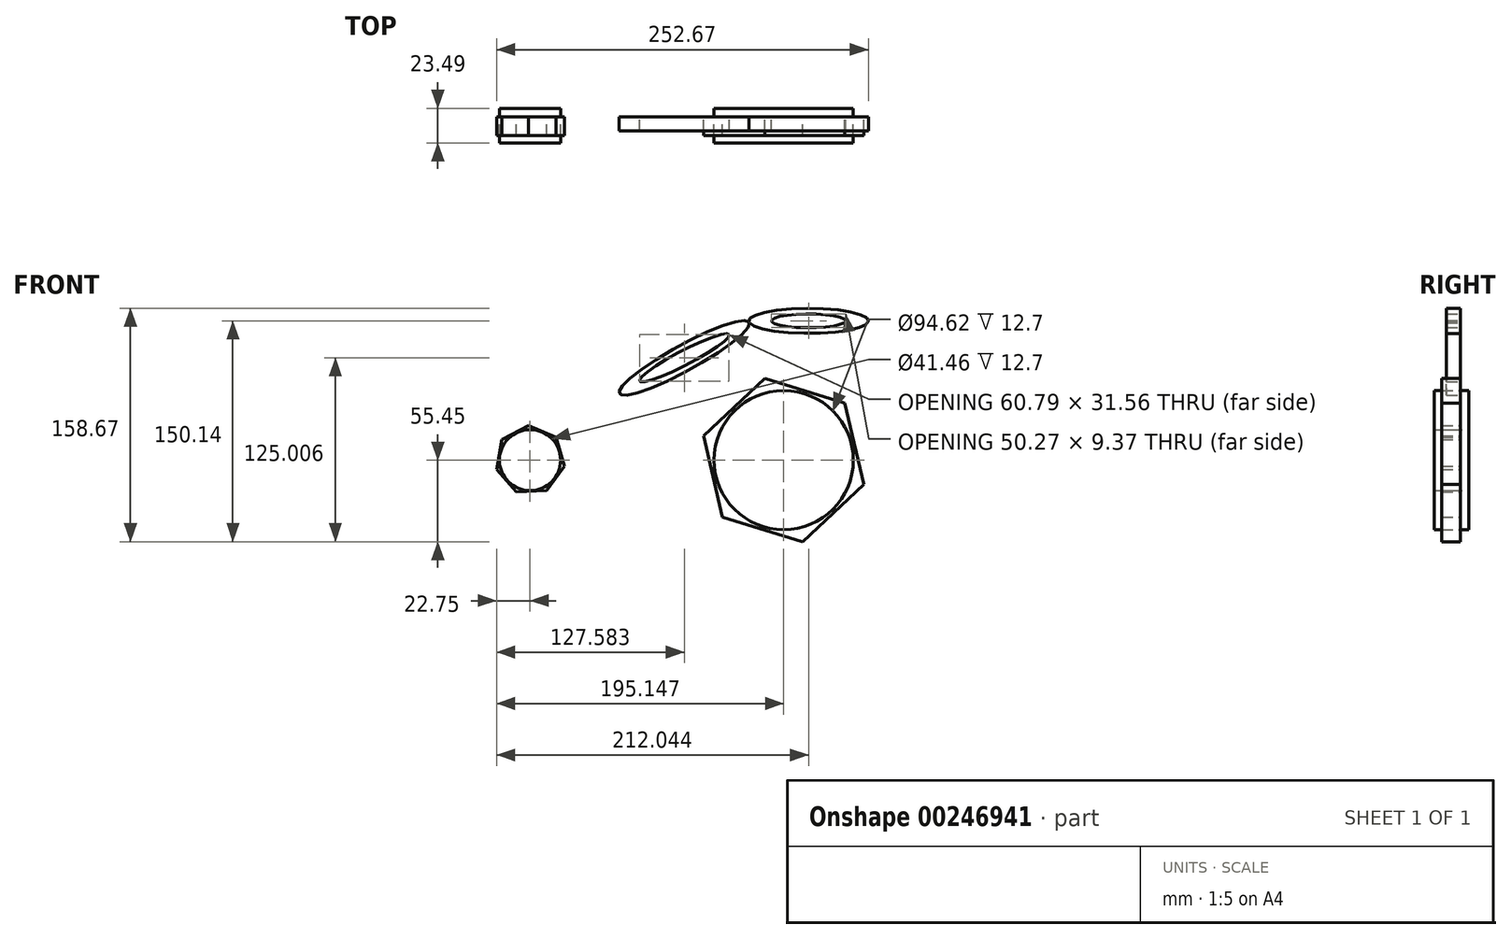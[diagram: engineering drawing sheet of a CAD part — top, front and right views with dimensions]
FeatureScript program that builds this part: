
annotation { "Feature Type Name" : "Feature", "Feature Type Description" : "" }
export const myFeature = defineFeature(function(context is Context, id is Id, definition is map)
    precondition{}
    {
        {
            var Q0;
            Q0=qCreatedBy(makeId("Front.planeOp"),FACE);
            var sketch = newSketch(context, id + "F0", { "sketchPlane" : qUnion([Q0])});
            skCircle(sketch, "E0", {"center": v(0, 0) * mm, "radius": 20.73 * mm});
            skCircle(sketch, "E1", {"center": v(172.4, 0) * mm, "radius": 47.3 * mm});
            skCircle(sketch, "E2.cCircle", {"center": v(0, 0) * mm, "radius": 23.62 * mm, "construction": true});
            skLineSegment(sketch, "E2.0", {"start": v(23.26, -4.14) * mm, "end": v(11.27, -20.76) * mm});
            skLineSegment(sketch, "E2.1", {"start": v(11.27, -20.76) * mm, "end": v(-9.2, -21.76) * mm});
            skLineSegment(sketch, "E2.2", {"start": v(-9.2, -21.76) * mm, "end": v(-22.75, -6.37) * mm});
            skLineSegment(sketch, "E2.3", {"start": v(-22.75, -6.37) * mm, "end": v(-19.16, 13.82) * mm});
            skLineSegment(sketch, "E2.4", {"start": v(-19.16, 13.82) * mm, "end": v(-1.14, 23.6) * mm});
            skLineSegment(sketch, "E2.5", {"start": v(-1.14, 23.6) * mm, "end": v(17.74, 15.6) * mm});
            skLineSegment(sketch, "E2.6", {"start": v(17.74, 15.6) * mm, "end": v(23.26, -4.14) * mm});
            skCircle(sketch, "E3.cCircle", {"center": v(172.4, 0) * mm, "radius": 56.91 * mm, "construction": true});
            skLineSegment(sketch, "E3.0", {"start": v(226.83, -16.62) * mm, "end": v(185.22, -55.45) * mm});
            skLineSegment(sketch, "E3.1", {"start": v(185.22, -55.45) * mm, "end": v(130.8, -38.83) * mm});
            skLineSegment(sketch, "E3.2", {"start": v(130.8, -38.83) * mm, "end": v(117.96, 16.62) * mm});
            skLineSegment(sketch, "E3.3", {"start": v(117.96, 16.62) * mm, "end": v(159.57, 55.45) * mm});
            skLineSegment(sketch, "E3.4", {"start": v(159.57, 55.45) * mm, "end": v(214, 38.83) * mm});
            skLineSegment(sketch, "E3.5", {"start": v(214, 38.83) * mm, "end": v(226.83, -16.62) * mm});
            skSolve(sketch);
        }
        {
            var Q0;
            Q0 = qSketchRegion(id + "F0", true);
            extrude(context, id + "F1", {"entities" : qUnion([Q0]), "depth" : 12.7 * mm});
        }
        {
            var Q0;
            Q0=makeQuery(id+"F0.imprint","IMPRINT",FACE,{"disambiguationData":[TD([[makeQuery(id+"F0.imprint","IMPRINT",EDGE,{"derivedFrom":sQuery(id+"F0.wireOp",EDGE,"E0")}),1.0]])]});
            var Q1;
            Q1=makeQuery(id+"F0.imprint","IMPRINT",FACE,{"disambiguationData":[TD([[makeQuery(id+"F0.imprint","IMPRINT",EDGE,{"derivedFrom":sQuery(id+"F0.wireOp",EDGE,"E1")}),1.0]])]});
            extrude(context, id + "F2", {"entities" : qUnion([Q0, Q1]), "depth" : 17.78 * mm, "hasSecondDirection" : true, "secondDirectionOppositeDirection" : true, "secondDirectionDepth" : 5.7 * mm});
        }
        {
            var Q0;
            Q0=qCreatedBy(makeId("Front.planeOp"),FACE);
            var sketch = newSketch(context, id + "F3", { "sketchPlane" : qUnion([Q0])});
            skEllipse(sketch, "E4", {"center": v(189.3, 94.7) * mm, "majorRadius": 40.62 * mm, "minorRadius": 8.53 * mm, "majorAxis": v(1, 0)});
            skEllipse(sketch, "E5", {"center": v(104.83, 69.56) * mm, "majorRadius": 50.36 * mm, "minorRadius": 8.8 * mm, "majorAxis": v(0.88, 0.48)});
            skEllipse(sketch, "E6", {"center": v(104.83, 69.56) * mm, "majorRadius": 34.25 * mm, "minorRadius": 4.95 * mm, "majorAxis": v(0.89, 0.46)});
            skEllipse(sketch, "E7", {"center": v(189.3, 94.7) * mm, "majorRadius": 25.13 * mm, "minorRadius": 4.69 * mm, "majorAxis": v(1, 0)});
            skSolve(sketch);
        }
        {
            var Q0;
            Q0 = qSketchRegion(id + "F3", true);
            extrude(context, id + "F4", {"entities" : qUnion([Q0]), "depth" : 9.6 * mm});
        }
    });
